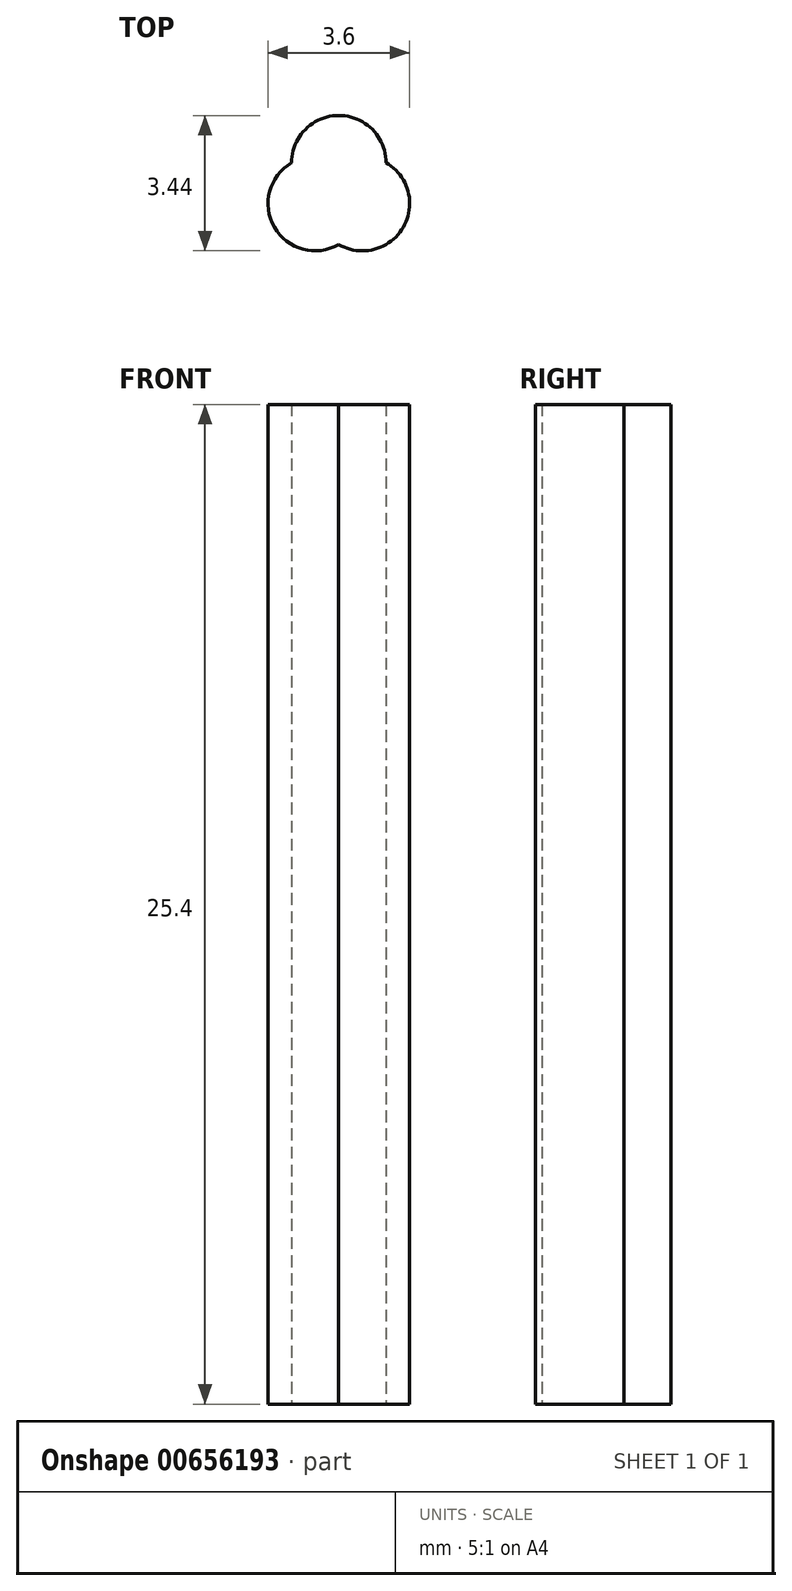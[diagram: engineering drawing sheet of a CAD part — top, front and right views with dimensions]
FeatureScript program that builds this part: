
annotation { "Feature Type Name" : "Feature", "Feature Type Description" : "" }
export const myFeature = defineFeature(function(context is Context, id is Id, definition is map)
    precondition{}
    {
        {
            var Q0;
            Q0=qCreatedBy(makeId("Top.planeOp"),FACE);
            var sketch = newSketch(context, id + "F0", { "sketchPlane" : qUnion([Q0])});
            skCircle(sketch, "E0", {"center": v(0, 0) * mm, "radius": 1.2 * mm});
            skCircle(sketch, "E1", {"center": v(-0.6, 1.04) * mm, "radius": 1.2 * mm});
            skCircle(sketch, "E2", {"center": v(-1.2, 0) * mm, "radius": 1.2 * mm});
            skSolve(sketch);
        }
        {
            var Q0;
            {var subQ0=sQuery(id+"F0.wireOp",EDGE,"E1");var subQ1=sQuery(id+"F0.wireOp",EDGE,"E0");var subQ2=makeQuery(id+"F0.imprint","INTERSECT",VERTEX,{"disambiguationData":[OD(0.0)],"derivedFrom":[subQ1,subQ0]});Q0=makeQuery(id+"F0.imprint","IMPRINT",FACE,{"disambiguationData":[TD([[makeQuery(id+"F0.imprint","IMPRINT",EDGE,{"disambiguationData":[TD([[subQ2,-1.0]])],"derivedFrom":subQ1}),-1.0]])]});}
            var Q1;
            {var subQ0=sQuery(id+"F0.wireOp",EDGE,"E2");var subQ1=sQuery(id+"F0.wireOp",EDGE,"E0");var subQ2=makeQuery(id+"F0.imprint","INTERSECT",VERTEX,{"disambiguationData":[OD(1.0)],"derivedFrom":[subQ1,subQ0]});Q1=makeQuery(id+"F0.imprint","IMPRINT",FACE,{"disambiguationData":[TD([[makeQuery(id+"F0.imprint","IMPRINT",EDGE,{"disambiguationData":[TD([[subQ2,-1.0]])],"derivedFrom":subQ1}),-1.0]])]});}
            var Q2;
            {var subQ0=sQuery(id+"F0.wireOp",EDGE,"E2");var subQ1=sQuery(id+"F0.wireOp",EDGE,"E0");var subQ2=makeQuery(id+"F0.imprint","INTERSECT",VERTEX,{"disambiguationData":[OD(1.0)],"derivedFrom":[subQ1,subQ0]});Q2=makeQuery(id+"F0.imprint","IMPRINT",FACE,{"disambiguationData":[TD([[makeQuery(id+"F0.imprint","IMPRINT",EDGE,{"disambiguationData":[TD([[subQ2,-1.0]])],"derivedFrom":subQ1}),1.0]])]});}
            var Q3;
            {var subQ0=sQuery(id+"F0.wireOp",EDGE,"E1");var subQ1=sQuery(id+"F0.wireOp",EDGE,"E0");var subQ2=makeQuery(id+"F0.imprint","INTERSECT",VERTEX,{"disambiguationData":[OD(0.0)],"derivedFrom":[subQ1,subQ0]});Q3=makeQuery(id+"F0.imprint","IMPRINT",FACE,{"disambiguationData":[TD([[makeQuery(id+"F0.imprint","IMPRINT",EDGE,{"disambiguationData":[TD([[subQ2,-1.0]])],"derivedFrom":subQ1}),1.0]])]});}
            var Q4;
            {var subQ0=sQuery(id+"F0.wireOp",EDGE,"E1");var subQ1=sQuery(id+"F0.wireOp",EDGE,"E0");var subQ2=makeQuery(id+"F0.imprint","INTERSECT",VERTEX,{"disambiguationData":[OD(0.0)],"derivedFrom":[subQ1,subQ0]});Q4=makeQuery(id+"F0.imprint","IMPRINT",FACE,{"disambiguationData":[TD([[makeQuery(id+"F0.imprint","IMPRINT",EDGE,{"disambiguationData":[TD([[subQ2,1.0]])],"derivedFrom":subQ1}),1.0]])]});}
            var Q5;
            {var subQ0=sQuery(id+"F0.wireOp",EDGE,"E2");var subQ1=sQuery(id+"F0.wireOp",EDGE,"E0");var subQ2=makeQuery(id+"F0.imprint","INTERSECT",VERTEX,{"disambiguationData":[OD(0.0)],"derivedFrom":[subQ1,subQ0]});Q5=makeQuery(id+"F0.imprint","IMPRINT",FACE,{"disambiguationData":[TD([[makeQuery(id+"F0.imprint","IMPRINT",EDGE,{"disambiguationData":[TD([[subQ2,1.0]])],"derivedFrom":subQ1}),1.0]])]});}
            var Q6;
            {var subQ0=sQuery(id+"F0.wireOp",EDGE,"E2");var subQ1=sQuery(id+"F0.wireOp",EDGE,"E0");var subQ2=makeQuery(id+"F0.imprint","INTERSECT",VERTEX,{"disambiguationData":[OD(0.0)],"derivedFrom":[subQ1,subQ0]});Q6=makeQuery(id+"F0.imprint","IMPRINT",FACE,{"disambiguationData":[TD([[makeQuery(id+"F0.imprint","IMPRINT",EDGE,{"disambiguationData":[TD([[subQ2,1.0]])],"derivedFrom":subQ1}),-1.0]])]});}
            extrude(context, id + "F1", {"entities" : qUnion([Q0, Q1, Q2, Q3, Q4, Q5, Q6]), "depth" : 25.4 * mm, "offsetDistance" : 25.4 * mm});
        }
    });
